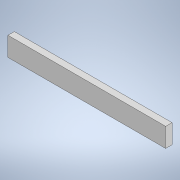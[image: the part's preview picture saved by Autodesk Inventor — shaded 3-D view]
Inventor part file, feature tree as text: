
AUTODESK INVENTOR PART (.ipt)
format: ipt  version: 2021 (Build 250183000, 183)  size: 123,904 bytes
history: native  units: in
note: dims shown in document units (in); Inventor stores cm internally (conversion verified against a paired STEP export)
features: extrude x2, sketch x2, pattern_linear x1, projected_geometry x1
ambient origin geometry x8: Origin, YZ Plane, XZ Plane, XY Plane, X Axis, Y Axis, Z Axis, Center Point
bodies: Solid1 (feature_tree)
feature tree (6):
  extrude  "Extrusion1"  Depth=0.375in
  extrude  "Extrusion2"  Depth=0.125in
  pattern_linear  "Rectangular Pattern1"  Spacing1=0.082in  [1 undecoded]
  sketch  "Sketch1"  dims[d0=3.085in d1=0.375in]
  sketch  "Sketch2"  dims[d2=0.125in d3=0.0in d4=0.125in d5=0.082in d6=0.0312in d7=0.0in d8=4.3307in d10=0.25in]
  projected_geometry  "Projected Loop1"
note: 1 required parameter value undecoded (feature->parameter linkage not recoverable at this tier; creation-order binding heuristic only, values carry confidence <= 0.55)
